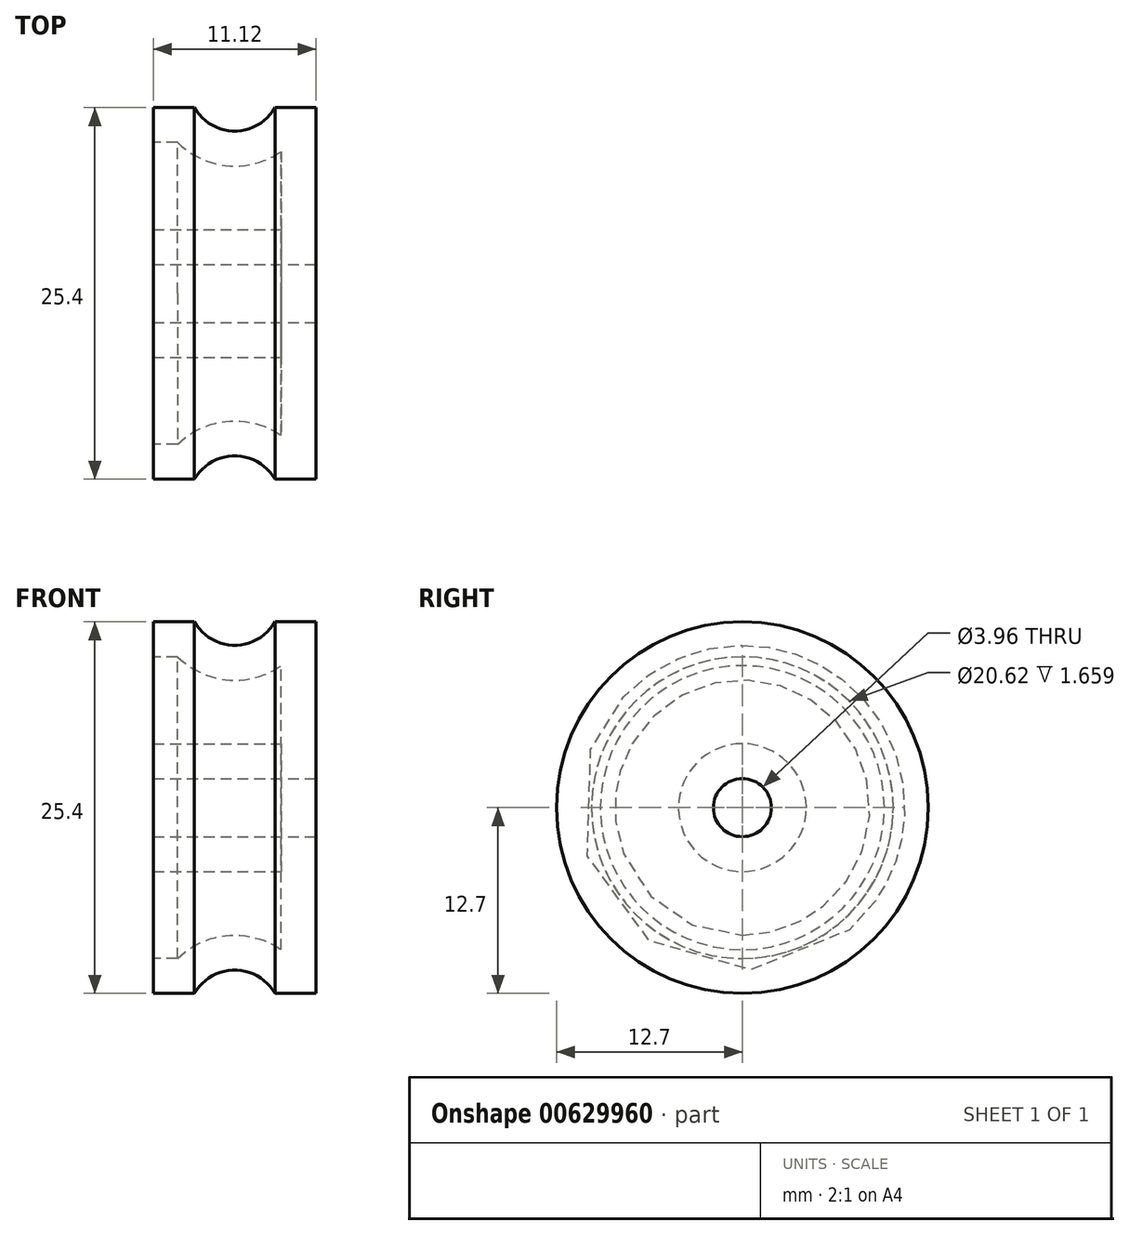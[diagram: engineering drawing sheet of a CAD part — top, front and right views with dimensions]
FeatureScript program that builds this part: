
annotation { "Feature Type Name" : "Feature", "Feature Type Description" : "" }
export const myFeature = defineFeature(function(context is Context, id is Id, definition is map)
    precondition{}
    {
        {
            var Q0;
            Q0=qCreatedBy(makeId("Front.planeOp"),FACE);
            var sketch = newSketch(context, id + "F0", { "sketchPlane" : qUnion([Q0])});
            skLineSegment(sketch, "E0.bottom", {"start": v(-5.56, 0) * mm, "end": v(5.56, 0) * mm, "construction": true});
            skLineSegment(sketch, "E0.top", {"start": v(-5.56, 12.7) * mm, "end": v(-2.76, 12.7) * mm});
            skLineSegment(sketch, "E0.left", {"start": v(-5.56, 0) * mm, "end": v(-5.56, 12.7) * mm});
            skLineSegment(sketch, "E0.right", {"start": v(5.56, 0) * mm, "end": v(5.56, 12.7) * mm});
            skArc(sketch, "E1", {"start": v(-2.76, 12.7) * mm, "mid": v(0, 11.1) * mm, "end": v(2.76, 12.7) * mm});
            skLineSegment(sketch, "E2.trimOffspring", {"start": v(2.76, 12.7) * mm, "end": v(5.56, 12.7) * mm});
            skLineSegment(sketch, "E3", {"start": v(-5.56, 0) * mm, "end": v(5.56, 0) * mm});
            skSolve(sketch);
        }
        {
            var Q0;
            Q0=makeQuery(id+"F0.imprint","IMPRINT",FACE,{"disambiguationData":[TD([[makeQuery(id+"F0.imprint","IMPRINT",EDGE,{"derivedFrom":sQuery(id+"F0.wireOp",EDGE,"E0.top")}),-1.0]])]});
            var Q1;
            Q1=sQuery(id+"F0.wireOp",EDGE,"E3");
            revolve(context, id + "F1", {"entities" : qUnion([Q0]), "axis" : qUnion([Q1]), "revolveType" : RevolveType.FULL});
        }
        {
            var Q0;
            Q0=makeQuery(id+"F1.opRevolve","SWEPT_FACE",FACE,{"disambiguationData":[OSD([sQuery(id+"F0.wireOp",EDGE,"E0.right")])]});
            var sketch = newSketch(context, id + "F2", { "sketchPlane" : qUnion([Q0])});
            skCircle(sketch, "E4", {"center": v(0, 0) * mm, "radius": 1.98 * mm});
            skSolve(sketch);
        }
        {
            var Q0;
            Q0 = qSketchRegion(id + "F2", true);
            extrude(context, id + "F3", {"entities" : qUnion([Q0]), "operationType" : NewBodyOperationType.REMOVE, "endBound" : BoundingType.THROUGH_ALL, "oppositeDirection" : true, "depth" : 25.4 * mm, "offsetDistance" : 25.4 * mm});
        }
        {
            var Q0;
            Q0=makeQuery(id+"F1.opRevolve","SWEPT_FACE",FACE,{"disambiguationData":[OSD([sQuery(id+"F0.wireOp",EDGE,"E0.left")])]});
            shell(context, id + "F4", {"entities" : qUnion([Q0]), "thickness" : 2.4 * mm});
        }
    });
